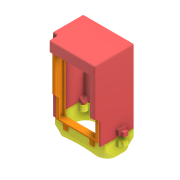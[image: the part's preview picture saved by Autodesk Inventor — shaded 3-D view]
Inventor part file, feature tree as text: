
AUTODESK INVENTOR PART (.ipt)
format: ipt  version: 2020.4 (Build 244396000, 396)  size: 1,463,296 bytes
history: native  units: mm
features: sketch x35, extrude x29, mirror x19, fillet x12, plane x12, other x9, chamfer x7, projected_geometry x6, revolve x3, boolean_combine x3, loft x3, hole x2, shell x1, pattern_circular x1, imported_body x1
ambient origin geometry x8: Origin, YZ Plane, XZ Plane, XY Plane, X Axis, Y Axis, Z Axis, Center Point
bodies: Body1 (feature_tree), Body2 (feature_tree), Body3 (feature_tree), Body4 (feature_tree), Body5 (feature_tree), Body6 (feature_tree)
feature tree (143):
  other  "housing"
  extrude  "BASE START"  Depth=0.3mm
  extrude  "Extrusion31"  Depth=0.3mm
  fillet  "Fillet12"  Radius=0.4mm
  fillet  "Fillet8"  Radius=5.4mm
  mirror  "Mirror9"
  mirror  "Mirror10"
  mirror  "Mirror11"
  mirror  "Mirror12"
  extrude  "Extrusion73"  TaperAngle=0.0deg  [1 undecoded]
  hole  "Hole2"  [1 undecoded]
  mirror  "Mirror30"
  mirror  "Mirror31"
  fillet  "Fillet44"  Radius=0.5mm
  other  "Base plane"
  other  "Housing plane 1"
  extrude  "HOUSING START"  Depth=0.3mm
  extrude  "Extrusion2"  Depth=10.0mm TaperAngle=0.0deg
  extrude  "Extrusion4"  TaperAngle=0.0deg  [1 undecoded]
  extrude  "Extrusion5"  Depth=0.3mm
  extrude  "Extrusion6"  Depth=7.0mm TaperAngle=0.0deg
  extrude  "Extrusion7"  Depth=2.0mm
  plane  "Work Plane46"
  extrude  "Extrusion84"  Depth=0.02mm
  fillet  "Fillet46"  [1 undecoded]
  mirror  "Mirror43"
  extrude  "Extrusion33"  TaperAngle=0.0deg  [1 undecoded]
  extrude  "Extrusion34"  Depth=10.0mm TaperAngle=0.0deg
  fillet  "Fillet11"  Radius=0.3mm
  chamfer  "Chamfer16"  Distance=0.1mm
  chamfer  "Chamfer17"  Distance=0.2mm
  other  "Cover plane"
  extrude  "COVER START"  Depth=0.3mm
  extrude  "Extrusion42"  Depth=3.0mm TaperAngle=0.0deg
  extrude  "Extrusion43"  Depth=8.0mm
  extrude  "Extrusion44"  Depth=0.3mm
  chamfer  "Chamfer7"  Distance=2.0mm
  chamfer  "Chamfer4"  Distance=5.0mm
  plane  "Work Plane44"
  plane  "Work Plane45"
  plane  "Work Plane54"
  plane  "Work Plane53"
  extrude  "Extrusion78"  Depth=0.4mm
  revolve  "Revolution2"  [1 undecoded]
  mirror  "Mirror37"
  mirror  "Mirror35"
  boolean_combine  "Combine11"
  extrude  "Extrusion79"  Depth=0.15mm
  mirror  "Mirror38"
  chamfer  "Chamfer10"  Distance=0.6mm
  chamfer  "Chamfer15"  Distance=0.25mm
  extrude  "Extrusion93"  TaperAngle=0.0deg  [1 undecoded]
  extrude  "CAP START"  Depth=3.0mm
  hole  "Hole1"  [1 undecoded]
  plane  "Work Plane35"
  extrude  "Extrusion40"  Depth=0.15mm
  shell  "Shell2"  Thickness=2.0mm
  boolean_combine  "Combine8"
  extrude  "Extrusion75"  Depth=0.15mm
  mirror  "Mirror39"
  mirror  "Mirror40"
  chamfer  "Chamfer18"  Angle=90.0deg  [1 undecoded]
  plane  "Work Plane48"
  extrude  "Extrusion87"  TaperAngle=0.0deg  [1 undecoded]
  extrude  "Extrusion88"  Depth=0.15mm
  extrude  "Extrusion89"  Depth=0.3mm
  mirror  "Mirror45"
  mirror  "Mirror46"
  mirror  "Mirror47"
  fillet  "Fillet40"  Radius=1.2mm
  fillet  "Fillet41"  Radius=0.3mm
  fillet  "Fillet20"  [1 undecoded]
  fillet  "Fillet24"  Radius=0.1mm
  fillet  "Fillet42"  Radius=1.0mm
  fillet  "Fillet43"  Radius=0.3mm
  fillet  "Fillet45"  [1 undecoded]
  plane  "Work Plane12"
  extrude  "CLAW START"  Depth=0.3mm
  plane  "Work Plane37"
  loft  "Loft15"
  boolean_combine  "Combine10"
  plane  "Work Plane38"
  loft  "Loft19"
  plane  "Work Plane43"
  loft  "Loft17"
  mirror  "Mirror23"
  revolve  "Revolution3"  [1 undecoded]
  mirror  "Mirror44"
  revolve  "Revolution4"  [1 undecoded]
  mirror  "Mirror49"
  extrude  "Extrusion86"  TaperAngle=90.0deg  [1 undecoded]
  pattern_circular  "Circular Pattern1"  [2 undecoded]
  extrude  "Extrusion90"  Depth=2.0mm
  mirror  "Mirror50"
  extrude  "Extrusion92"  Depth=3.0mm
  sketch  "Sketch1"  dims[d1=0.85mm d3=0.3mm]
  sketch  "Sketch2"  dims[d4=0.3mm d7=0.3mm d8=0.4mm d14=5.4mm d15=0.0mm]
  sketch  "Sketch4"  dims[d17=0.3mm d19=0.0mm]
  projected_geometry  "Projected Loop3"
  projected_geometry  "Projected Loop4"
  sketch  "Sketch5"  dims[d25=0.3mm d26=0.0mm d27=0.5mm d28=0.0mm]
  sketch  "Sketch6"  dims[d29=0.3mm d30=0.3mm]
  sketch  "Sketch7"  dims[d31=1.7mm d32=10.0mm d33=0.0mm]
  sketch  "Sketch14"  dims[d35=0.3mm d36=0.0mm]
  imported_body  "base"
  sketch  "Sketch21"  dims[d47=0.4mm d92=0.3mm]
  other  "cap"
  other  "claw"
  sketch  "Sketch28"  dims[d95=0.0mm d142=7.0mm d143=0.0mm]
  sketch  "Sketch36"  dims[d166=2.0mm d168=2.1mm]
  sketch  "Sketch42"  dims[d169=15.0mm d170=0.0mm d240=0.02mm d243=0.0mm d244=90.0deg]
  sketch  "Sketch52"  dims[d298=0.6mm d362=0.0mm]
  sketch  "Sketch54"  dims[d369=0.6mm d370=10.0mm d371=0.0mm d382=0.3mm d383=0.1mm d384=0.0mm]
  sketch  "Sketch55"  dims[d385=0.25mm]
  projected_geometry  "Projected Loop22"
  projected_geometry  "Projected Loop23"
  sketch  "Sketch56"  dims[d386=0.2mm d387=0.2mm d388=0.0mm]
  sketch  "Sketch57"  dims[d389=0.3mm d391=0.3mm]
  other  "cover"
  sketch  "Sketch58"  dims[d392=0.0mm d393=2.3mm d394=0.0mm d395=3.0mm d396=2.4mm d397=0.0mm d398=3.0mm]
  projected_geometry  "Projected Loop24"
  sketch  "Sketch64"  dims[d413=0.2mm d414=0.8mm]
  plane  "Work Plane36"
  other  "Edges8"
  sketch  "Sketch82"  dims[d431=3.264mm d432=6.0mm d433=5.0mm d434=6.0mm d435=14.3117mm d436=8.0mm d437=45.0deg d438=6.6mm]
  sketch  "Sketch83"  dims[d439=4.8mm d440=0.0mm d444=0.3mm]
  sketch  "Sketch93"  dims[d447=0.5mm]
  sketch  "Sketch94"  dims[d448=0.1mm]
  sketch  "Sketch97"  dims[d449=0.1mm]
  sketch  "Sketch101"  dims[d454=0.1mm]
  sketch  "Sketch105"  dims[d455=0.1mm]
  other  "tool_pegs"
  sketch  "Sketch112"  dims[d456=0.3mm d457=2.0mm d458=0.0mm]
  sketch  "Sketch113"  dims[d459=0.3mm]
  sketch  "Sketch114"  dims[d460=0.0mm]
  sketch  "Sketch115"  dims[d461=0.8mm d463=5.0mm d464=0.0mm]
  sketch  "Sketch116"  dims[d465=0.4mm d466=0.4mm]
  sketch  "Sketch117"  dims[d467=0.8mm d468=0.0mm d487=13.962634mm d488=0.6mm d489=11.34464mm]
  sketch  "Sketch118"  dims[d510=0.3mm d512=0.15mm d515=0.6mm d516=1.15mm d517=3.490659mm]
  sketch  "Sketch119"  dims[d582=5.0mm]
  sketch  "Sketch120"  dims[d583=-3.0mm]
  sketch  "Sketch122"  dims[d611=0.4mm d625=0.25mm d637=0.0mm d638=90.0deg d639=-0.3mm d640=3.0mm d647=1.0mm d648=1.6mm d649=2.0mm d650=4.0mm d651=0.0mm d652=90.0deg d653=0.0mm d654=90.0deg d692=1.15mm d716=0.3mm d718=1.2mm d719=0.0mm d720=1.0mm d721=5.0mm d722=1.0mm d723=2.845mm d724=90.0deg d725=0.75mm d726=60.0deg d731=0.3mm d732=0.0mm d740=0.1mm d741=1.0mm d742=0.0mm d743=0.3mm d744=0.0mm d746=0.3mm d747=0.3mm d748=0.3mm d749=0.3mm d750=0.3mm d768=0.3mm d769=90.0deg d776=0.65mm d777=2.0mm d778=3.490659mm d791=0.95mm d792=2.0mm d793=3.490659mm d807=3.0mm d813=-1.6mm d821=0.85mm d822=2.0mm d823=3.490659mm d824=0.85mm d825=2.0mm d826=3.490659mm d831=1.0mm d832=0.0mm d833=0.3mm d867=0.4mm d868=180.0deg d869=0.4mm d870=0.6mm d871=3.8mm d872=10.0mm d873=0.0mm d874=20.0mm d875=180.0deg d878=1.8mm d879=0.6mm d880=0.0mm d881=0.3mm d883=0.5mm d884=0.0mm d885=1.2mm d887=0.8mm d891=0.3mm d892=0.0mm d893=0.1mm d894=0.2mm d896=180.0deg d897=2.0mm d898=0.0mm d899=90.0deg d900=0.0mm d901=90.0deg d902=0.65mm d903=2.0mm d904=45.0deg d910=0.3mm d911=0.3mm d912=0.05mm d913=0.55mm d914=1.6mm d915=0.15mm d916=7.0mm d917=0.0mm d925=1.5mm d926=0.3mm d927=0.3mm d928=0.0mm d929=0.2mm d930=0.15mm d931=0.0mm d936=0.05mm d937=0.05mm d502=0.5mm d503=0.872665mm d504=0.5mm d505=0.872665mm d694=0.5mm d695=0.872665mm d696=0.5mm d697=0.872665mm d814=0.5mm d815=0.872665mm d816=0.5mm d817=0.872665mm d818=0.5mm d819=0.872665mm d820=0.5mm d1064=0.5mm d1065=0.872665mm d1066=0.5mm d1067=0.872665mm d1076=0.5mm d1077=0.872665mm d1078=0.5mm d1079=0.872665mm d1189=0.872665mm d1190=0.872665mm]
  projected_geometry  "Project Cut Edges1"
note: 17 required parameter values undecoded (feature->parameter linkage not recoverable at this tier; creation-order binding heuristic only, values carry confidence <= 0.55)